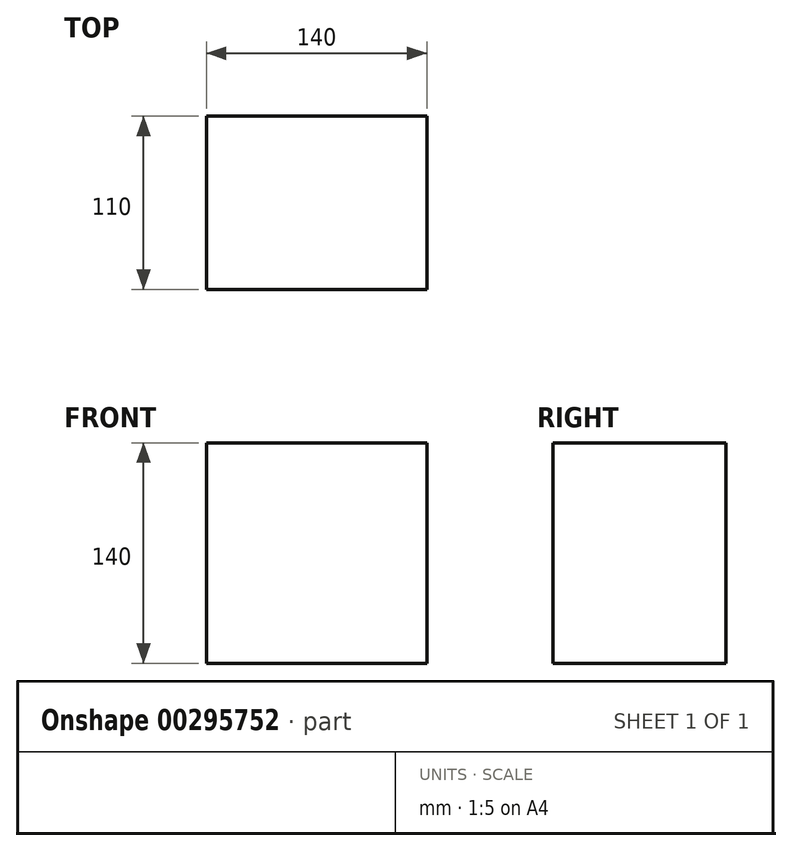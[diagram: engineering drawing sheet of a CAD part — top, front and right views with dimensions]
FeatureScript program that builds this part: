
annotation { "Feature Type Name" : "Feature", "Feature Type Description" : "" }
export const myFeature = defineFeature(function(context is Context, id is Id, definition is map)
    precondition{}
    {
        {
            var Q0;
            Q0=qCreatedBy(makeId("Top.planeOp"),FACE);
            var sketch = newSketch(context, id + "F0", { "sketchPlane" : qUnion([Q0])});
            skLineSegment(sketch, "E0.bottom", {"start": v(-110.47, 49.38) * mm, "end": v(29.53, 49.38) * mm});
            skLineSegment(sketch, "E0.top", {"start": v(-110.47, -60.62) * mm, "end": v(29.53, -60.62) * mm});
            skLineSegment(sketch, "E0.left", {"start": v(-110.47, 49.38) * mm, "end": v(-110.47, -60.62) * mm});
            skLineSegment(sketch, "E0.right", {"start": v(29.53, 49.38) * mm, "end": v(29.53, -60.62) * mm});
            skSolve(sketch);
        }
        {
            var Q0;
            Q0 = qSketchRegion(id + "F0", true);
            extrude(context, id + "F1", {"entities" : qUnion([Q0]), "depth" : 140 * mm});
        }
    });
